# Revit family: SL510 Slim_SlimECO 2-Flg. m.Seitenteile – Laibungsmontage
name_source: partatom
category: Türen
revit_build: Autodesk Revit 2018 (Build: 20190510_1515(x64)
units: mm (PartAtom-declared; Revit-internal decimal feet)

## family parameters
Basisbauteil = Wand
Beim Laden mit Abzugskörper schneiden = Nein
Gemeinsam genutzt = Nein
Immer vertikal = Ja
OmniClass-Nummer = 23.30.10.00
OmniClass-Titel = Doors
Raumberechnungspunkt = Nein

## types (2) — shared parameters
Familienversion = 1.0
Glasstärke = 8 mm  [stored 0.0262467 ft]
Höhe ab FBOK berechnen = Ja
Montagefuge Breite = 5 mm  [stored 0.0164042 ft]
Wandabschluss = Nach Basisbauteil
zero-valued in all types: IFC_Glasflächenanteil, IFC_Luftdurchlässigkeit, IFC_Schallschutzklasse

## per-type parameters (varying)
| type | Dicke | Kollisionskörper | Oberlicht | Oberlicht Höhe | Oberlicht zweigeteilt |
| SL510 Slim_SlimECO 2-Flg. m.Seitenteile u.Oberlichte – Laibungsmontage | 20 mm  [stored 0.0656168 ft] | Nein | Ja | 500 mm  [stored 1.64042 ft] | Nein |
| SL510 Slim_SlimECO 2-Flg. m.Seitenteile – Laibungsmontage | 0 mm  [stored 0 ft] | Ja | Nein | 0 mm  [stored 0 ft] | Ja |

note: [stored X ft] marks values corroborated as IEEE doubles in the binary element streams (Revit-internal decimal feet)
